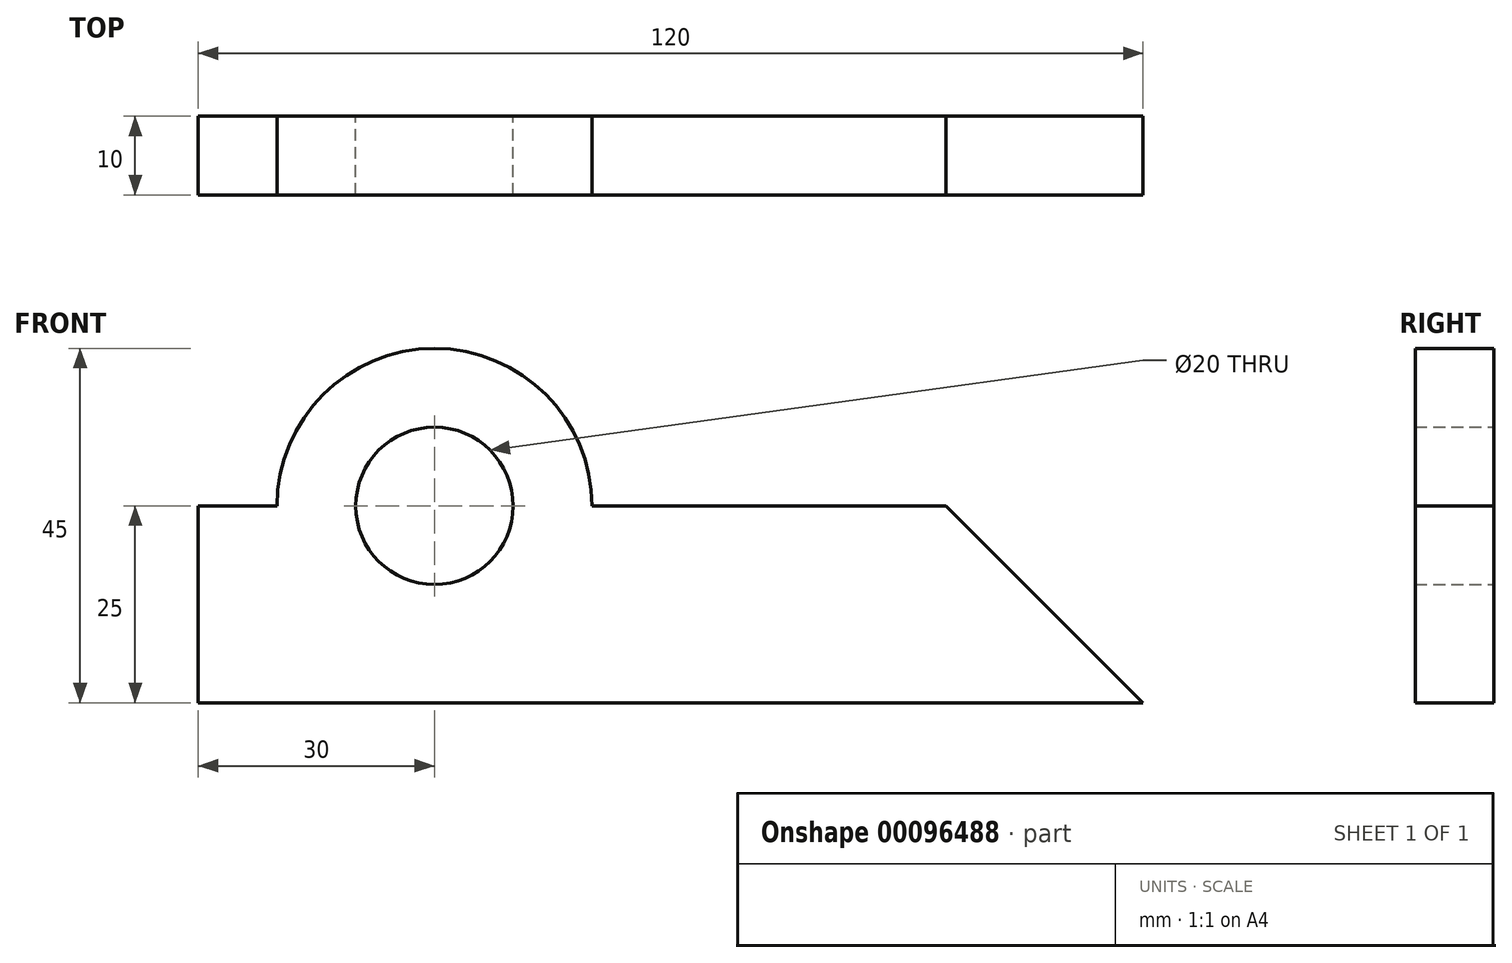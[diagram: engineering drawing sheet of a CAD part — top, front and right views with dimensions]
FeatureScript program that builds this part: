
annotation { "Feature Type Name" : "Feature", "Feature Type Description" : "" }
export const myFeature = defineFeature(function(context is Context, id is Id, definition is map)
    precondition{}
    {
        {
            var Q0;
            Q0=qCreatedBy(makeId("Front.planeOp"),FACE);
            var sketch = newSketch(context, id + "F0", { "sketchPlane" : qUnion([Q0])});
            skLineSegment(sketch, "E0.bottom", {"start": v(0, 0) * mm, "end": v(120, 0) * mm, "construction": true});
            skLineSegment(sketch, "E0.top", {"start": v(0, 0) * mm, "end": v(120, 0) * mm, "construction": true});
            skLineSegment(sketch, "E0.left", {"start": v(0, 0) * mm, "end": v(0, 0) * mm});
            skLineSegment(sketch, "E0.right", {"start": v(120, 0) * mm, "end": v(120, 0) * mm});
            skLineSegment(sketch, "E1", {"start": v(0, 0) * mm, "end": v(0, 25) * mm});
            skLineSegment(sketch, "E2", {"start": v(0, 0) * mm, "end": v(120, 0) * mm});
            skLineSegment(sketch, "E3", {"start": v(120, 0) * mm, "end": v(95, 25) * mm});
            skLineSegment(sketch, "E4", {"start": v(0, 25) * mm, "end": v(10, 25) * mm});
            skLineSegment(sketch, "E5", {"start": v(95, 25) * mm, "end": v(50, 25) * mm});
            skArc(sketch, "E6", {"start": v(50, 25) * mm, "mid": v(30, 45) * mm, "end": v(10, 25) * mm});
            skCircle(sketch, "E7", {"center": v(30, 25) * mm, "radius": 10 * mm});
            skSolve(sketch);
        }
        {
            var Q0;
            Q0=makeQuery(id+"F0.imprint","IMPRINT",FACE,{"disambiguationData":[TD([[makeQuery(id+"F0.imprint","IMPRINT",EDGE,{"derivedFrom":sQuery(id+"F0.wireOp",EDGE,"E1")}),-1.0]])]});
            extrude(context, id + "F1", {"entities" : qUnion([Q0]), "depth" : 10 * mm});
        }
    });
